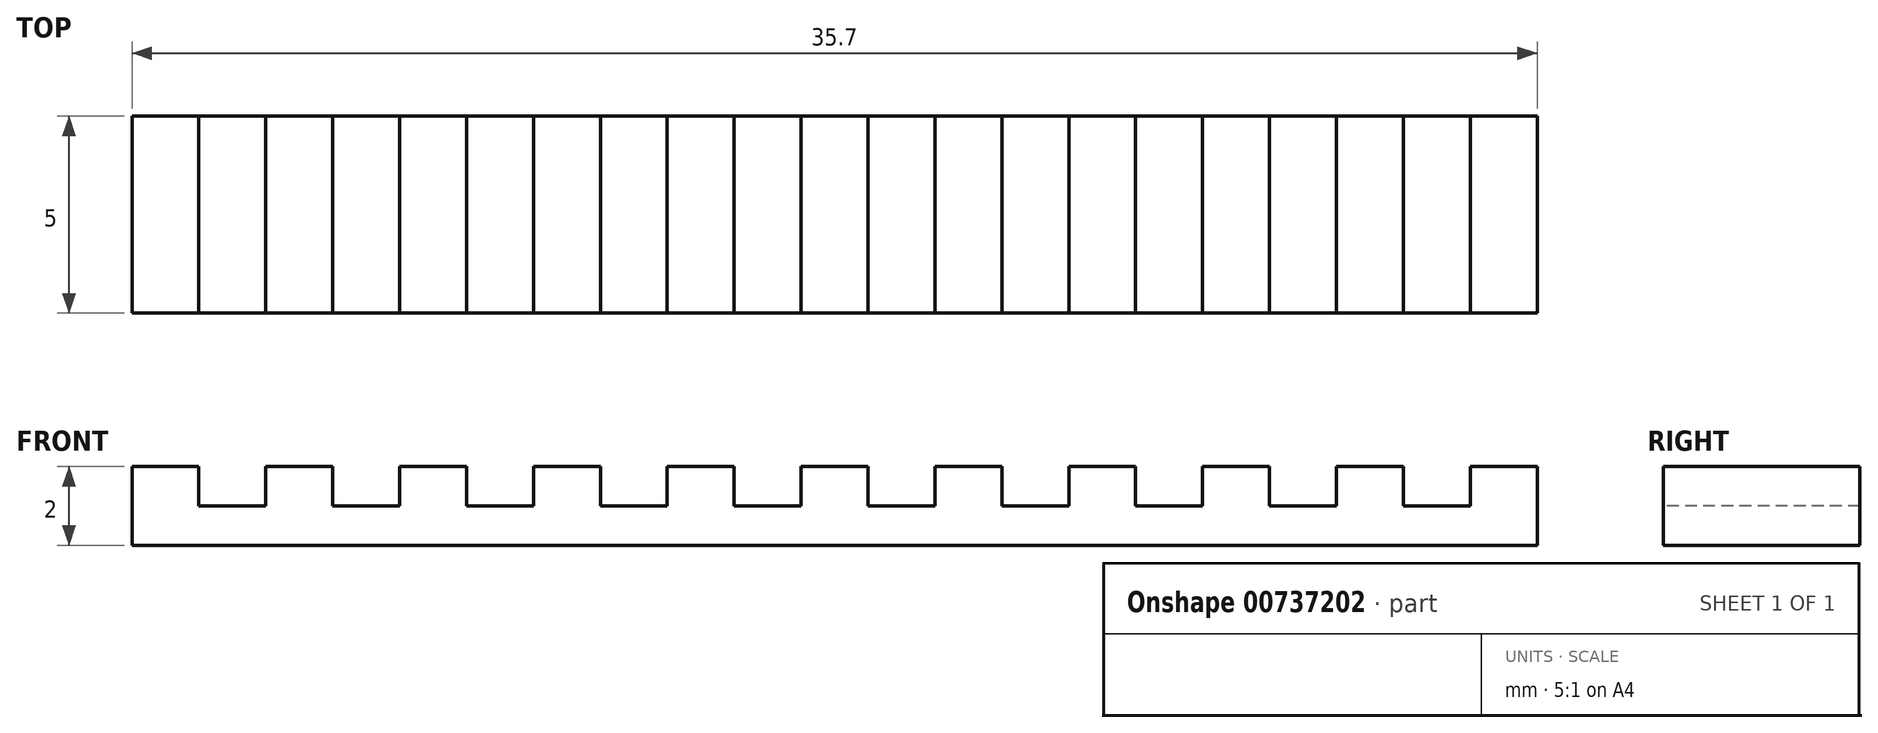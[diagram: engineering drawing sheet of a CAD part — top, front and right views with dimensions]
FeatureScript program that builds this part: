
annotation { "Feature Type Name" : "Feature", "Feature Type Description" : "" }
export const myFeature = defineFeature(function(context is Context, id is Id, definition is map)
    precondition{}
    {
        {
            var Q0;
            Q0=qCreatedBy(makeId("Front.planeOp"),FACE);
            var sketch = newSketch(context, id + "F0", { "sketchPlane" : qUnion([Q0])});
            skLineSegment(sketch, "E0.bottom", {"start": v(0, 0) * mm, "end": v(-35.7, 0) * mm});
            skLineSegment(sketch, "E0.top", {"start": v(0, 2) * mm, "end": v(-35.7, 2) * mm});
            skLineSegment(sketch, "E0.left", {"start": v(0, 0) * mm, "end": v(0, 2) * mm});
            skLineSegment(sketch, "E0.right", {"start": v(-35.7, 0) * mm, "end": v(-35.7, 2) * mm});
            skSolve(sketch);
        }
        {
            var Q0;
            Q0=makeQuery(id+"F0.imprint","IMPRINT",FACE,{"disambiguationData":[TD([[makeQuery(id+"F0.imprint","IMPRINT",EDGE,{"derivedFrom":sQuery(id+"F0.wireOp",EDGE,"E0.bottom")}),-1.0]])]});
            extrude(context, id + "F1", {"entities" : qUnion([Q0]), "depth" : 5 * mm, "offsetDistance" : 25 * mm});
        }
        {
            var Q0;
            Q0=makeQuery(id+"F1.opExtrude","CAP_FACE",FACE,{"disambiguationData":[OSD([sQuery(id+"F0.wireOp",EDGE,"E0.bottom"),sQuery(id+"F0.wireOp",EDGE,"E0.top"),sQuery(id+"F0.wireOp",EDGE,"E0.left"),sQuery(id+"F0.wireOp",EDGE,"E0.right")])],"isStart":false});
            var sketch = newSketch(context, id + "F2", { "sketchPlane" : qUnion([Q0])});
            skLineSegment(sketch, "E1.bottom", {"start": v(-34, 2) * mm, "end": v(-32.3, 2) * mm});
            skLineSegment(sketch, "E1.top", {"start": v(-34, 1) * mm, "end": v(-32.3, 1) * mm});
            skLineSegment(sketch, "E1.left", {"start": v(-34, 2) * mm, "end": v(-34, 1) * mm});
            skLineSegment(sketch, "E1.right", {"start": v(-32.3, 2) * mm, "end": v(-32.3, 1) * mm});
            skLineSegment(sketch, "E2.1.0.0", {"start": v(-30.6, 2) * mm, "end": v(-28.9, 2) * mm});
            skLineSegment(sketch, "E2.1.0.1", {"start": v(-28.9, 2) * mm, "end": v(-28.9, 1) * mm});
            skLineSegment(sketch, "E2.1.0.2", {"start": v(-30.6, 1) * mm, "end": v(-28.9, 1) * mm});
            skLineSegment(sketch, "E2.1.0.3", {"start": v(-30.6, 2) * mm, "end": v(-30.6, 1) * mm});
            skLineSegment(sketch, "E2.2.0.0", {"start": v(-27.2, 2) * mm, "end": v(-25.5, 2) * mm});
            skLineSegment(sketch, "E2.2.0.1", {"start": v(-25.5, 2) * mm, "end": v(-25.5, 1) * mm});
            skLineSegment(sketch, "E2.2.0.2", {"start": v(-27.2, 1) * mm, "end": v(-25.5, 1) * mm});
            skLineSegment(sketch, "E2.2.0.3", {"start": v(-27.2, 2) * mm, "end": v(-27.2, 1) * mm});
            skLineSegment(sketch, "E2.3.0.0", {"start": v(-23.8, 2) * mm, "end": v(-22.1, 2) * mm});
            skLineSegment(sketch, "E2.3.0.1", {"start": v(-22.1, 2) * mm, "end": v(-22.1, 1) * mm});
            skLineSegment(sketch, "E2.3.0.2", {"start": v(-23.8, 1) * mm, "end": v(-22.1, 1) * mm});
            skLineSegment(sketch, "E2.3.0.3", {"start": v(-23.8, 2) * mm, "end": v(-23.8, 1) * mm});
            skLineSegment(sketch, "E2.4.0.0", {"start": v(-20.4, 2) * mm, "end": v(-18.7, 2) * mm});
            skLineSegment(sketch, "E2.4.0.1", {"start": v(-18.7, 2) * mm, "end": v(-18.7, 1) * mm});
            skLineSegment(sketch, "E2.4.0.2", {"start": v(-20.4, 1) * mm, "end": v(-18.7, 1) * mm});
            skLineSegment(sketch, "E2.4.0.3", {"start": v(-20.4, 2) * mm, "end": v(-20.4, 1) * mm});
            skLineSegment(sketch, "E2.5.0.0", {"start": v(-17, 2) * mm, "end": v(-15.3, 2) * mm});
            skLineSegment(sketch, "E2.5.0.1", {"start": v(-15.3, 2) * mm, "end": v(-15.3, 1) * mm});
            skLineSegment(sketch, "E2.5.0.2", {"start": v(-17, 1) * mm, "end": v(-15.3, 1) * mm});
            skLineSegment(sketch, "E2.5.0.3", {"start": v(-17, 2) * mm, "end": v(-17, 1) * mm});
            skLineSegment(sketch, "E2.6.0.0", {"start": v(-13.6, 2) * mm, "end": v(-11.9, 2) * mm});
            skLineSegment(sketch, "E2.6.0.1", {"start": v(-11.9, 2) * mm, "end": v(-11.9, 1) * mm});
            skLineSegment(sketch, "E2.6.0.2", {"start": v(-13.6, 1) * mm, "end": v(-11.9, 1) * mm});
            skLineSegment(sketch, "E2.6.0.3", {"start": v(-13.6, 2) * mm, "end": v(-13.6, 1) * mm});
            skLineSegment(sketch, "E2.direction1", {"start": v(-34, 1) * mm, "end": v(-30.6, 1) * mm, "construction": true});
            skLineSegment(sketch, "E3.0.7.0", {"start": v(-10.2, 2) * mm, "end": v(-8.5, 2) * mm});
            skLineSegment(sketch, "E3.3.7.0", {"start": v(-8.5, 2) * mm, "end": v(-8.5, 1) * mm});
            skLineSegment(sketch, "E3.6.7.0", {"start": v(-10.2, 1) * mm, "end": v(-8.5, 1) * mm});
            skLineSegment(sketch, "E3.9.7.0", {"start": v(-10.2, 2) * mm, "end": v(-10.2, 1) * mm});
            skLineSegment(sketch, "E3.0.8.0", {"start": v(-6.8, 2) * mm, "end": v(-5.1, 2) * mm});
            skLineSegment(sketch, "E3.3.8.0", {"start": v(-5.1, 2) * mm, "end": v(-5.1, 1) * mm});
            skLineSegment(sketch, "E3.6.8.0", {"start": v(-6.8, 1) * mm, "end": v(-5.1, 1) * mm});
            skLineSegment(sketch, "E3.9.8.0", {"start": v(-6.8, 2) * mm, "end": v(-6.8, 1) * mm});
            skLineSegment(sketch, "E4.0.9.0", {"start": v(-3.4, 2) * mm, "end": v(-1.7, 2) * mm});
            skLineSegment(sketch, "E4.3.9.0", {"start": v(-1.7, 2) * mm, "end": v(-1.7, 1) * mm});
            skLineSegment(sketch, "E4.6.9.0", {"start": v(-3.4, 1) * mm, "end": v(-1.7, 1) * mm});
            skLineSegment(sketch, "E4.9.9.0", {"start": v(-3.4, 2) * mm, "end": v(-3.4, 1) * mm});
            skSolve(sketch);
        }
        {
            var Q0;
            Q0=makeQuery(id+"F2.imprint","IMPRINT",FACE,{"disambiguationData":[TD([[makeQuery(id+"F2.imprint","IMPRINT",EDGE,{"derivedFrom":sQuery(id+"F2.wireOp",EDGE,"E1.bottom")}),1.0]])]});
            var Q1;
            Q1=makeQuery(id+"F2.imprint","IMPRINT",FACE,{"disambiguationData":[TD([[makeQuery(id+"F2.imprint","IMPRINT",EDGE,{"derivedFrom":sQuery(id+"F2.wireOp",EDGE,"E2.1.0.0")}),1.0]])]});
            var Q2;
            Q2=makeQuery(id+"F2.imprint","IMPRINT",FACE,{"disambiguationData":[TD([[makeQuery(id+"F2.imprint","IMPRINT",EDGE,{"derivedFrom":sQuery(id+"F2.wireOp",EDGE,"E2.2.0.0")}),1.0]])]});
            var Q3;
            Q3=makeQuery(id+"F2.imprint","IMPRINT",FACE,{"disambiguationData":[TD([[makeQuery(id+"F2.imprint","IMPRINT",EDGE,{"derivedFrom":sQuery(id+"F2.wireOp",EDGE,"E2.3.0.0")}),1.0]])]});
            var Q4;
            Q4=makeQuery(id+"F2.imprint","IMPRINT",FACE,{"disambiguationData":[TD([[makeQuery(id+"F2.imprint","IMPRINT",EDGE,{"derivedFrom":sQuery(id+"F2.wireOp",EDGE,"E2.4.0.0")}),1.0]])]});
            var Q5;
            Q5=makeQuery(id+"F2.imprint","IMPRINT",FACE,{"disambiguationData":[TD([[makeQuery(id+"F2.imprint","IMPRINT",EDGE,{"derivedFrom":sQuery(id+"F2.wireOp",EDGE,"E2.5.0.0")}),1.0]])]});
            var Q6;
            Q6=makeQuery(id+"F2.imprint","IMPRINT",FACE,{"disambiguationData":[TD([[makeQuery(id+"F2.imprint","IMPRINT",EDGE,{"derivedFrom":sQuery(id+"F2.wireOp",EDGE,"E2.6.0.0")}),1.0]])]});
            extrude(context, id + "F3", {"entities" : qUnion([Q0, Q1, Q2, Q3, Q4, Q5, Q6]), "operationType" : NewBodyOperationType.REMOVE, "oppositeDirection" : true, "depth" : 5 * mm, "offsetDistance" : 25 * mm});
        }
        {
            var Q0;
            Q0=makeQuery(id+"F2.imprint","IMPRINT",FACE,{"disambiguationData":[TD([[makeQuery(id+"F2.imprint","IMPRINT",EDGE,{"derivedFrom":sQuery(id+"F2.wireOp",EDGE,"E3.0.7.0")}),1.0]])]});
            var Q1;
            Q1=makeQuery(id+"F2.imprint","IMPRINT",FACE,{"disambiguationData":[TD([[makeQuery(id+"F2.imprint","IMPRINT",EDGE,{"derivedFrom":sQuery(id+"F2.wireOp",EDGE,"E3.0.8.0")}),1.0]])]});
            var Q2;
            Q2=makeQuery(id+"F2.imprint","IMPRINT",FACE,{"disambiguationData":[TD([[makeQuery(id+"F2.imprint","IMPRINT",EDGE,{"derivedFrom":sQuery(id+"F2.wireOp",EDGE,"E4.0.9.0")}),1.0]])]});
            extrude(context, id + "F4", {"entities" : qUnion([Q0, Q1, Q2]), "operationType" : NewBodyOperationType.REMOVE, "oppositeDirection" : true, "depth" : 5 * mm, "offsetDistance" : 25 * mm});
        }
    });
